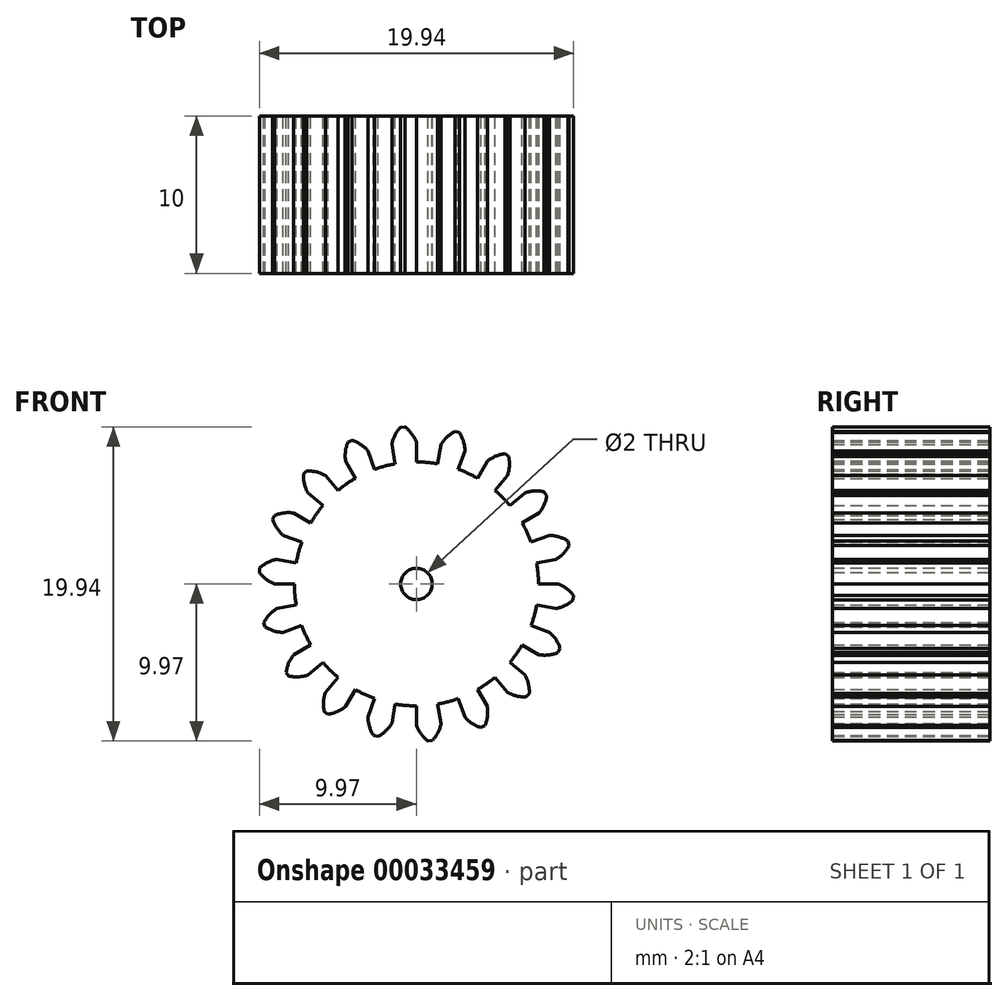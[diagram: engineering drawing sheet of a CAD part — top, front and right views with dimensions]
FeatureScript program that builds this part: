
annotation { "Feature Type Name" : "Feature", "Feature Type Description" : "" }
export const myFeature = defineFeature(function(context is Context, id is Id, definition is map)
    precondition{}
    {
        {
            var Q0;
            Q0=qCreatedBy(makeId("Front.planeOp"),FACE);
            var sketch = newSketch(context, id + "F0", { "sketchPlane" : qUnion([Q0])});
            skArc(sketch, "E0", {"start": v(-1.35, 7.63) * mm, "mid": v(-2, 7.49) * mm, "end": v(-2.65, 7.28) * mm});
            skLineSegment(sketch, "E1", {"start": v(0, 7.75) * mm, "end": v(0, 9) * mm});
            skArc(sketch, "E2", {"start": v(0, 9) * mm, "mid": v(-0.3, 9.54) * mm, "end": v(-0.73, 9.97) * mm});
            skArc(sketch, "E3.0.MirrorCS", {"start": v(-1.56, 8.86) * mm, "mid": v(-1.36, 9.44) * mm, "end": v(-1.02, 9.95) * mm});
            skLineSegment(sketch, "E4.0.MirrorCS", {"start": v(-1.35, 7.63) * mm, "end": v(-1.56, 8.86) * mm});
            skLineSegment(sketch, "E5", {"start": v(-1.02, 9.95) * mm, "end": v(-0.73, 9.97) * mm});
            skPoint(sketch, "E6.orphan", {"position": v(-2.26, 12.8) * mm});
            skPoint(sketch, "E7.orphan", {"position": v(0, 13) * mm});
            skArc(sketch, "E8.1.0", {"start": v(-4.5, 7.8) * mm, "mid": v(-4.51, 8.4) * mm, "end": v(-4.36, 9) * mm});
            skLineSegment(sketch, "E8.1.1", {"start": v(-2.65, 7.28) * mm, "end": v(-3.08, 8.46) * mm});
            skLineSegment(sketch, "E8.1.2", {"start": v(-3.88, 6.71) * mm, "end": v(-4.5, 7.8) * mm});
            skArc(sketch, "E8.1.3", {"start": v(-3.08, 8.46) * mm, "mid": v(-3.54, 8.86) * mm, "end": v(-4.1, 9.12) * mm});
            skLineSegment(sketch, "E8.1.4", {"start": v(-4.36, 9) * mm, "end": v(-4.1, 9.12) * mm});
            skArc(sketch, "E8.2.0", {"start": v(-6.9, 5.79) * mm, "mid": v(-7.11, 6.36) * mm, "end": v(-7.17, 6.97) * mm});
            skLineSegment(sketch, "E8.2.1", {"start": v(-4.98, 5.94) * mm, "end": v(-5.79, 6.9) * mm});
            skLineSegment(sketch, "E8.2.2", {"start": v(-5.94, 4.98) * mm, "end": v(-6.9, 5.79) * mm});
            skArc(sketch, "E8.2.3", {"start": v(-5.79, 6.9) * mm, "mid": v(-6.36, 7.11) * mm, "end": v(-6.97, 7.17) * mm});
            skLineSegment(sketch, "E8.2.4", {"start": v(-7.17, 6.97) * mm, "end": v(-6.97, 7.17) * mm});
            skArc(sketch, "E8.3.0", {"start": v(-8.46, 3.08) * mm, "mid": v(-8.86, 3.54) * mm, "end": v(-9.12, 4.1) * mm});
            skLineSegment(sketch, "E8.3.1", {"start": v(-6.71, 3.88) * mm, "end": v(-7.8, 4.5) * mm});
            skLineSegment(sketch, "E8.3.2", {"start": v(-7.28, 2.65) * mm, "end": v(-8.46, 3.08) * mm});
            skArc(sketch, "E8.3.3", {"start": v(-7.8, 4.5) * mm, "mid": v(-8.4, 4.51) * mm, "end": v(-9, 4.36) * mm});
            skLineSegment(sketch, "E8.3.4", {"start": v(-9.12, 4.1) * mm, "end": v(-9, 4.36) * mm});
            skArc(sketch, "E8.4.0", {"start": v(-9, 0) * mm, "mid": v(-9.54, 0.3) * mm, "end": v(-9.97, 0.73) * mm});
            skLineSegment(sketch, "E8.4.1", {"start": v(-7.63, 1.35) * mm, "end": v(-8.86, 1.56) * mm});
            skLineSegment(sketch, "E8.4.2", {"start": v(-7.75, 0) * mm, "end": v(-9, 0) * mm});
            skArc(sketch, "E8.4.3", {"start": v(-8.86, 1.56) * mm, "mid": v(-9.44, 1.36) * mm, "end": v(-9.95, 1.02) * mm});
            skLineSegment(sketch, "E8.4.4", {"start": v(-9.97, 0.73) * mm, "end": v(-9.95, 1.02) * mm});
            skArc(sketch, "E8.5.0", {"start": v(-8.46, -3.08) * mm, "mid": v(-9.06, -2.98) * mm, "end": v(-9.62, -2.73) * mm});
            skLineSegment(sketch, "E8.5.1", {"start": v(-7.63, -1.35) * mm, "end": v(-8.86, -1.56) * mm});
            skLineSegment(sketch, "E8.5.2", {"start": v(-7.28, -2.65) * mm, "end": v(-8.46, -3.08) * mm});
            skArc(sketch, "E8.5.3", {"start": v(-8.86, -1.56) * mm, "mid": v(-9.34, -1.95) * mm, "end": v(-9.7, -2.45) * mm});
            skLineSegment(sketch, "E8.5.4", {"start": v(-9.62, -2.73) * mm, "end": v(-9.7, -2.45) * mm});
            skArc(sketch, "E8.6.0", {"start": v(-6.9, -5.79) * mm, "mid": v(-7.5, -5.9) * mm, "end": v(-8.1, -5.85) * mm});
            skLineSegment(sketch, "E8.6.1", {"start": v(-6.71, -3.87) * mm, "end": v(-7.8, -4.5) * mm});
            skLineSegment(sketch, "E8.6.2", {"start": v(-5.94, -4.98) * mm, "end": v(-6.9, -5.79) * mm});
            skArc(sketch, "E8.6.3", {"start": v(-7.8, -4.5) * mm, "mid": v(-8.11, -5.03) * mm, "end": v(-8.27, -5.62) * mm});
            skLineSegment(sketch, "E8.6.4", {"start": v(-8.1, -5.85) * mm, "end": v(-8.27, -5.62) * mm});
            skArc(sketch, "E8.7.0", {"start": v(-4.5, -7.8) * mm, "mid": v(-5.03, -8.11) * mm, "end": v(-5.62, -8.27) * mm});
            skLineSegment(sketch, "E8.7.1", {"start": v(-4.98, -5.94) * mm, "end": v(-5.79, -6.9) * mm});
            skLineSegment(sketch, "E8.7.2", {"start": v(-3.87, -6.71) * mm, "end": v(-4.5, -7.8) * mm});
            skArc(sketch, "E8.7.3", {"start": v(-5.79, -6.9) * mm, "mid": v(-5.9, -7.5) * mm, "end": v(-5.85, -8.1) * mm});
            skLineSegment(sketch, "E8.7.4", {"start": v(-5.62, -8.27) * mm, "end": v(-5.85, -8.1) * mm});
            skArc(sketch, "E8.8.0", {"start": v(-1.56, -8.86) * mm, "mid": v(-1.95, -9.34) * mm, "end": v(-2.45, -9.7) * mm});
            skLineSegment(sketch, "E8.8.1", {"start": v(-2.65, -7.28) * mm, "end": v(-3.08, -8.46) * mm});
            skLineSegment(sketch, "E8.8.2", {"start": v(-1.35, -7.63) * mm, "end": v(-1.56, -8.86) * mm});
            skArc(sketch, "E8.8.3", {"start": v(-3.08, -8.46) * mm, "mid": v(-2.98, -9.06) * mm, "end": v(-2.73, -9.62) * mm});
            skLineSegment(sketch, "E8.8.4", {"start": v(-2.45, -9.7) * mm, "end": v(-2.73, -9.62) * mm});
            skArc(sketch, "E8.9.0", {"start": v(1.56, -8.86) * mm, "mid": v(1.36, -9.44) * mm, "end": v(1.02, -9.95) * mm});
            skLineSegment(sketch, "E8.9.1", {"start": v(0, -7.75) * mm, "end": v(0, -9) * mm});
            skLineSegment(sketch, "E8.9.2", {"start": v(1.35, -7.63) * mm, "end": v(1.56, -8.86) * mm});
            skArc(sketch, "E8.9.3", {"start": v(0, -9) * mm, "mid": v(0.3, -9.54) * mm, "end": v(0.73, -9.97) * mm});
            skLineSegment(sketch, "E8.9.4", {"start": v(1.02, -9.95) * mm, "end": v(0.73, -9.97) * mm});
            skArc(sketch, "E8.10.0", {"start": v(4.5, -7.8) * mm, "mid": v(4.51, -8.4) * mm, "end": v(4.36, -9) * mm});
            skLineSegment(sketch, "E8.10.1", {"start": v(2.65, -7.28) * mm, "end": v(3.08, -8.46) * mm});
            skLineSegment(sketch, "E8.10.2", {"start": v(3.88, -6.71) * mm, "end": v(4.5, -7.8) * mm});
            skArc(sketch, "E8.10.3", {"start": v(3.08, -8.46) * mm, "mid": v(3.54, -8.86) * mm, "end": v(4.1, -9.12) * mm});
            skLineSegment(sketch, "E8.10.4", {"start": v(4.36, -9) * mm, "end": v(4.1, -9.12) * mm});
            skArc(sketch, "E8.11.0", {"start": v(6.9, -5.79) * mm, "mid": v(7.11, -6.36) * mm, "end": v(7.17, -6.97) * mm});
            skLineSegment(sketch, "E8.11.1", {"start": v(4.98, -5.94) * mm, "end": v(5.79, -6.9) * mm});
            skLineSegment(sketch, "E8.11.2", {"start": v(5.94, -4.98) * mm, "end": v(6.9, -5.79) * mm});
            skArc(sketch, "E8.11.3", {"start": v(5.79, -6.9) * mm, "mid": v(6.36, -7.11) * mm, "end": v(6.97, -7.17) * mm});
            skLineSegment(sketch, "E8.11.4", {"start": v(7.17, -6.97) * mm, "end": v(6.97, -7.17) * mm});
            skArc(sketch, "E8.12.0", {"start": v(8.46, -3.08) * mm, "mid": v(8.86, -3.54) * mm, "end": v(9.12, -4.1) * mm});
            skLineSegment(sketch, "E8.12.1", {"start": v(6.71, -3.88) * mm, "end": v(7.8, -4.5) * mm});
            skLineSegment(sketch, "E8.12.2", {"start": v(7.28, -2.65) * mm, "end": v(8.46, -3.08) * mm});
            skArc(sketch, "E8.12.3", {"start": v(7.8, -4.5) * mm, "mid": v(8.4, -4.51) * mm, "end": v(9, -4.36) * mm});
            skLineSegment(sketch, "E8.12.4", {"start": v(9.12, -4.1) * mm, "end": v(9, -4.36) * mm});
            skArc(sketch, "E8.13.0", {"start": v(9, 0) * mm, "mid": v(9.54, -0.3) * mm, "end": v(9.97, -0.73) * mm});
            skLineSegment(sketch, "E8.13.1", {"start": v(7.63, -1.35) * mm, "end": v(8.86, -1.56) * mm});
            skLineSegment(sketch, "E8.13.2", {"start": v(7.75, 0) * mm, "end": v(9, 0) * mm});
            skArc(sketch, "E8.13.3", {"start": v(8.86, -1.56) * mm, "mid": v(9.44, -1.36) * mm, "end": v(9.95, -1.02) * mm});
            skLineSegment(sketch, "E8.13.4", {"start": v(9.97, -0.73) * mm, "end": v(9.95, -1.02) * mm});
            skArc(sketch, "E8.14.0", {"start": v(8.46, 3.08) * mm, "mid": v(9.06, 2.98) * mm, "end": v(9.62, 2.73) * mm});
            skLineSegment(sketch, "E8.14.1", {"start": v(7.63, 1.35) * mm, "end": v(8.86, 1.56) * mm});
            skLineSegment(sketch, "E8.14.2", {"start": v(7.28, 2.65) * mm, "end": v(8.46, 3.08) * mm});
            skArc(sketch, "E8.14.3", {"start": v(8.86, 1.56) * mm, "mid": v(9.34, 1.95) * mm, "end": v(9.7, 2.45) * mm});
            skLineSegment(sketch, "E8.14.4", {"start": v(9.62, 2.73) * mm, "end": v(9.7, 2.45) * mm});
            skArc(sketch, "E8.15.0", {"start": v(6.9, 5.79) * mm, "mid": v(7.5, 5.9) * mm, "end": v(8.1, 5.85) * mm});
            skLineSegment(sketch, "E8.15.1", {"start": v(6.71, 3.87) * mm, "end": v(7.8, 4.5) * mm});
            skLineSegment(sketch, "E8.15.2", {"start": v(5.94, 4.98) * mm, "end": v(6.9, 5.79) * mm});
            skArc(sketch, "E8.15.3", {"start": v(7.8, 4.5) * mm, "mid": v(8.11, 5.03) * mm, "end": v(8.27, 5.62) * mm});
            skLineSegment(sketch, "E8.15.4", {"start": v(8.1, 5.85) * mm, "end": v(8.27, 5.62) * mm});
            skArc(sketch, "E8.16.0", {"start": v(4.5, 7.8) * mm, "mid": v(5.03, 8.11) * mm, "end": v(5.62, 8.27) * mm});
            skLineSegment(sketch, "E8.16.1", {"start": v(4.98, 5.94) * mm, "end": v(5.79, 6.9) * mm});
            skLineSegment(sketch, "E8.16.2", {"start": v(3.87, 6.71) * mm, "end": v(4.5, 7.8) * mm});
            skArc(sketch, "E8.16.3", {"start": v(5.79, 6.9) * mm, "mid": v(5.9, 7.5) * mm, "end": v(5.85, 8.1) * mm});
            skLineSegment(sketch, "E8.16.4", {"start": v(5.62, 8.27) * mm, "end": v(5.85, 8.1) * mm});
            skArc(sketch, "E8.17.0", {"start": v(1.56, 8.86) * mm, "mid": v(1.95, 9.34) * mm, "end": v(2.45, 9.7) * mm});
            skLineSegment(sketch, "E8.17.1", {"start": v(2.65, 7.28) * mm, "end": v(3.08, 8.46) * mm});
            skLineSegment(sketch, "E8.17.2", {"start": v(1.35, 7.63) * mm, "end": v(1.56, 8.86) * mm});
            skArc(sketch, "E8.17.3", {"start": v(3.08, 8.46) * mm, "mid": v(2.98, 9.06) * mm, "end": v(2.73, 9.62) * mm});
            skLineSegment(sketch, "E8.17.4", {"start": v(2.45, 9.7) * mm, "end": v(2.73, 9.62) * mm});
            skArc(sketch, "E9.trimOffspring", {"start": v(1.35, 7.63) * mm, "mid": v(0.68, 7.72) * mm, "end": v(0, 7.75) * mm});
            skArc(sketch, "E10.trimOffspring", {"start": v(3.88, 6.71) * mm, "mid": v(3.28, 7.02) * mm, "end": v(2.65, 7.28) * mm});
            skArc(sketch, "E11.trimOffspring", {"start": v(5.94, 4.98) * mm, "mid": v(5.48, 5.48) * mm, "end": v(4.98, 5.94) * mm});
            skArc(sketch, "E12.trimOffspring", {"start": v(7.28, 2.65) * mm, "mid": v(7.02, 3.28) * mm, "end": v(6.71, 3.87) * mm});
            skArc(sketch, "E13.trimOffspring", {"start": v(7.75, 0) * mm, "mid": v(7.72, 0.68) * mm, "end": v(7.63, 1.35) * mm});
            skArc(sketch, "E14.trimOffspring", {"start": v(7.28, -2.65) * mm, "mid": v(7.49, -2) * mm, "end": v(7.63, -1.35) * mm});
            skArc(sketch, "E15.trimOffspring", {"start": v(5.94, -4.98) * mm, "mid": v(6.35, -4.45) * mm, "end": v(6.71, -3.88) * mm});
            skArc(sketch, "E16.trimOffspring", {"start": v(3.87, -6.71) * mm, "mid": v(4.45, -6.35) * mm, "end": v(4.98, -5.94) * mm});
            skArc(sketch, "E17.trimOffspring", {"start": v(1.35, -7.63) * mm, "mid": v(2, -7.49) * mm, "end": v(2.65, -7.28) * mm});
            skArc(sketch, "E18.trimOffspring", {"start": v(-1.35, -7.63) * mm, "mid": v(-0.68, -7.72) * mm, "end": v(0, -7.75) * mm});
            skArc(sketch, "E19.trimOffspring", {"start": v(-3.87, -6.71) * mm, "mid": v(-3.28, -7.02) * mm, "end": v(-2.65, -7.28) * mm});
            skArc(sketch, "E20.trimOffspring", {"start": v(-5.94, -4.98) * mm, "mid": v(-5.48, -5.48) * mm, "end": v(-4.98, -5.94) * mm});
            skArc(sketch, "E21.trimOffspring", {"start": v(-7.28, -2.65) * mm, "mid": v(-7.02, -3.28) * mm, "end": v(-6.71, -3.87) * mm});
            skArc(sketch, "E22.trimOffspring", {"start": v(-7.75, 0) * mm, "mid": v(-7.72, -0.68) * mm, "end": v(-7.63, -1.35) * mm});
            skArc(sketch, "E23.trimOffspring", {"start": v(-7.28, 2.65) * mm, "mid": v(-7.49, 2) * mm, "end": v(-7.63, 1.35) * mm});
            skArc(sketch, "E24.trimOffspring", {"start": v(-5.94, 4.98) * mm, "mid": v(-6.35, 4.45) * mm, "end": v(-6.71, 3.87) * mm});
            skArc(sketch, "E25.trimOffspring", {"start": v(-3.88, 6.71) * mm, "mid": v(-4.45, 6.35) * mm, "end": v(-4.98, 5.94) * mm});
            skCircle(sketch, "E26", {"center": v(0, 0) * mm, "radius": 1 * mm});
            skSolve(sketch);
        }
        {
            var Q0;
            Q0=makeQuery(id+"F0.imprint","IMPRINT",FACE,{"disambiguationData":[TD([[makeQuery(id+"F0.imprint","IMPRINT",EDGE,{"derivedFrom":sQuery(id+"F0.wireOp",EDGE,"E0")}),1.0]])]});
            extrude(context, id + "F1", {"entities" : qUnion([Q0]), "depth" : 10 * mm});
        }
    });
